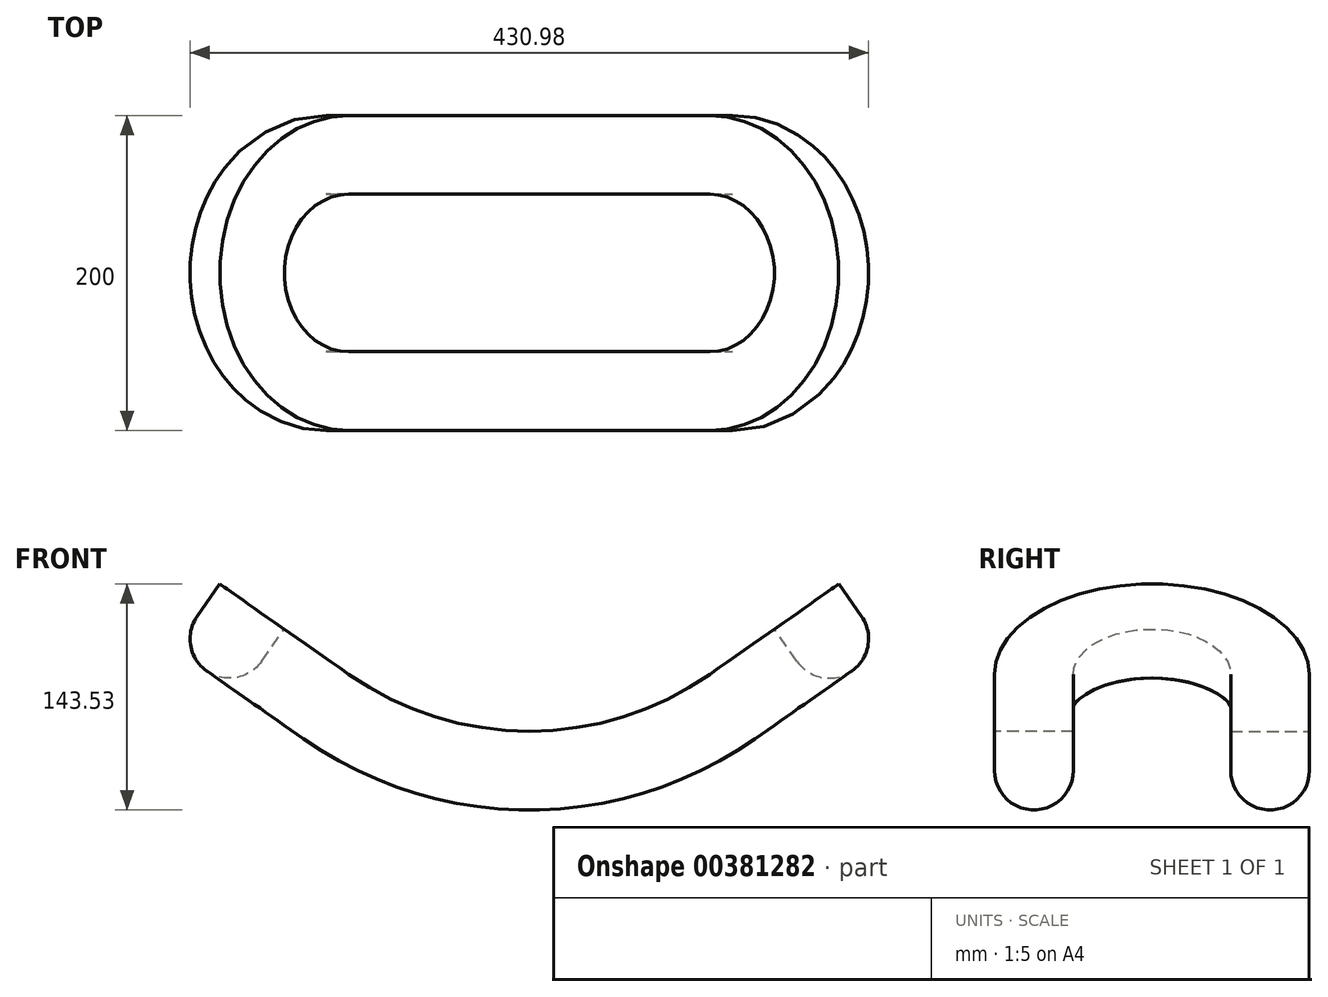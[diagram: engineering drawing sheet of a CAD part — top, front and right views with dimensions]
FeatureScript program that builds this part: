
annotation { "Feature Type Name" : "Feature", "Feature Type Description" : "" }
export const myFeature = defineFeature(function(context is Context, id is Id, definition is map)
    precondition{}
    {
        {
            var Q0;
            Q0=qCreatedBy(makeId("Front.planeOp"),FACE);
            var sketch = newSketch(context, id + "F0", { "sketchPlane" : qUnion([Q0])});
            skArc(sketch, "E0", {"start": v(0, 0) * mm, "mid": v(60.14, 9.26) * mm, "end": v(114.72, 36.17) * mm});
            skLineSegment(sketch, "E1", {"start": v(114.72, 36.17) * mm, "end": v(196.63, 93.53) * mm});
            skLineSegment(sketch, "E2", {"start": v(0, 200) * mm, "end": v(114.72, 36.17) * mm, "construction": true});
            skSolve(sketch);
        }
        {
            var Q0;
            Q0=sQuery(id+"F0.wireOp",EDGE,"E1");
            var Q1;
            Q1=sQuery(id+"F0.wireOp",EDGE,"E0");
            extrude(context, id + "F1", {"bodyType" : ToolBodyType.SURFACE, "surfaceEntities" : qUnion([Q0, Q1]), "depth" : 100 * mm});
        }
        {
            var Q0;
            Q0=makeQuery(id+"F1.opExtrude","SWEPT_FACE",FACE,{"disambiguationData":[OSD([sQuery(id+"F0.wireOp",EDGE,"E1")])]});
            var sketch = newSketch(context, id + "F2", { "sketchPlane" : qUnion([Q0])});
            skArc(sketch, "E3", {"start": v(214.72, 0) * mm, "mid": v(185.43, 70.71) * mm, "end": v(114.72, 100) * mm});
            skSolve(sketch);
        }
        {
            var Q0;
            Q0=qCreatedBy(makeId("Right.planeOp"),FACE);
            var sketch = newSketch(context, id + "F3", { "sketchPlane" : qUnion([Q0])});
            skLineSegment(sketch, "E4.bottom", {"start": v(-100, 0) * mm, "end": v(-50, 0) * mm});
            skLineSegment(sketch, "E4.top", {"start": v(-100, -25) * mm, "end": v(-50, -25) * mm, "construction": true});
            skLineSegment(sketch, "E4.left", {"start": v(-100, 0) * mm, "end": v(-100, -25) * mm});
            skLineSegment(sketch, "E4.right", {"start": v(-50, 0) * mm, "end": v(-50, -25) * mm});
            skArc(sketch, "E5", {"start": v(-100, -25) * mm, "mid": v(-75, -50) * mm, "end": v(-50, -25) * mm});
            skLineSegment(sketch, "E6", {"start": v(-100, 36.17) * mm, "end": v(-100, -51.05) * mm, "construction": true});
            skSolve(sketch);
        }
        {
            var Q0;
            Q0=makeQuery(id+"F3.imprint","IMPRINT",FACE,{"disambiguationData":[TD([[makeQuery(id+"F3.imprint","IMPRINT",EDGE,{"derivedFrom":sQuery(id+"F3.wireOp",EDGE,"E4.bottom")}),-1.0]])]});
            var Q1;
            Q1=makeQuery(id+"F1.opExtrude","CAP_EDGE",EDGE,{"disambiguationData":[OSD([sQuery(id+"F0.wireOp",EDGE,"E0")])],"isStart":false});
            var Q2;
            Q2=sQuery(id+"F2.wireOp",EDGE,"E3");
            sweep(context, id + "F4", {"profiles" : qUnion([Q0]), "path" : qUnion([Q1, Q2])});
        }
        {
            var Q0;
            Q0=makeQuery(id+"F4.opSweep","SWEPT_BODY",BODY,{"disambiguationData":[OSD([sQuery(id+"F2.wireOp",EDGE,"E3"),sQuery(id+"F3.wireOp",EDGE,"E4.bottom"),sQuery(id+"F3.wireOp",EDGE,"E4.left"),sQuery(id+"F3.wireOp",EDGE,"E4.right"),sQuery(id+"F3.wireOp",EDGE,"E5")])]});
            var Q1;
            Q1=qCreatedBy(makeId("Right.planeOp"),FACE);
            mirror(context, id + "F5", {"operationType" : NewBodyOperationType.ADD, "entities" : qUnion([Q0]), "mirrorPlane" : qUnion([Q1])});
        }
        {
            var Q0;
            Q0=makeQuery(id+"F4.opSweep","SWEPT_BODY",BODY,{"disambiguationData":[OSD([sQuery(id+"F2.wireOp",EDGE,"E3"),sQuery(id+"F3.wireOp",EDGE,"E4.bottom"),sQuery(id+"F3.wireOp",EDGE,"E4.left"),sQuery(id+"F3.wireOp",EDGE,"E4.right"),sQuery(id+"F3.wireOp",EDGE,"E5")])]});
            var Q1;
            Q1=qCreatedBy(makeId("Front.planeOp"),FACE);
            mirror(context, id + "F6", {"operationType" : NewBodyOperationType.ADD, "entities" : qUnion([Q0]), "mirrorPlane" : qUnion([Q1])});
        }
    });
